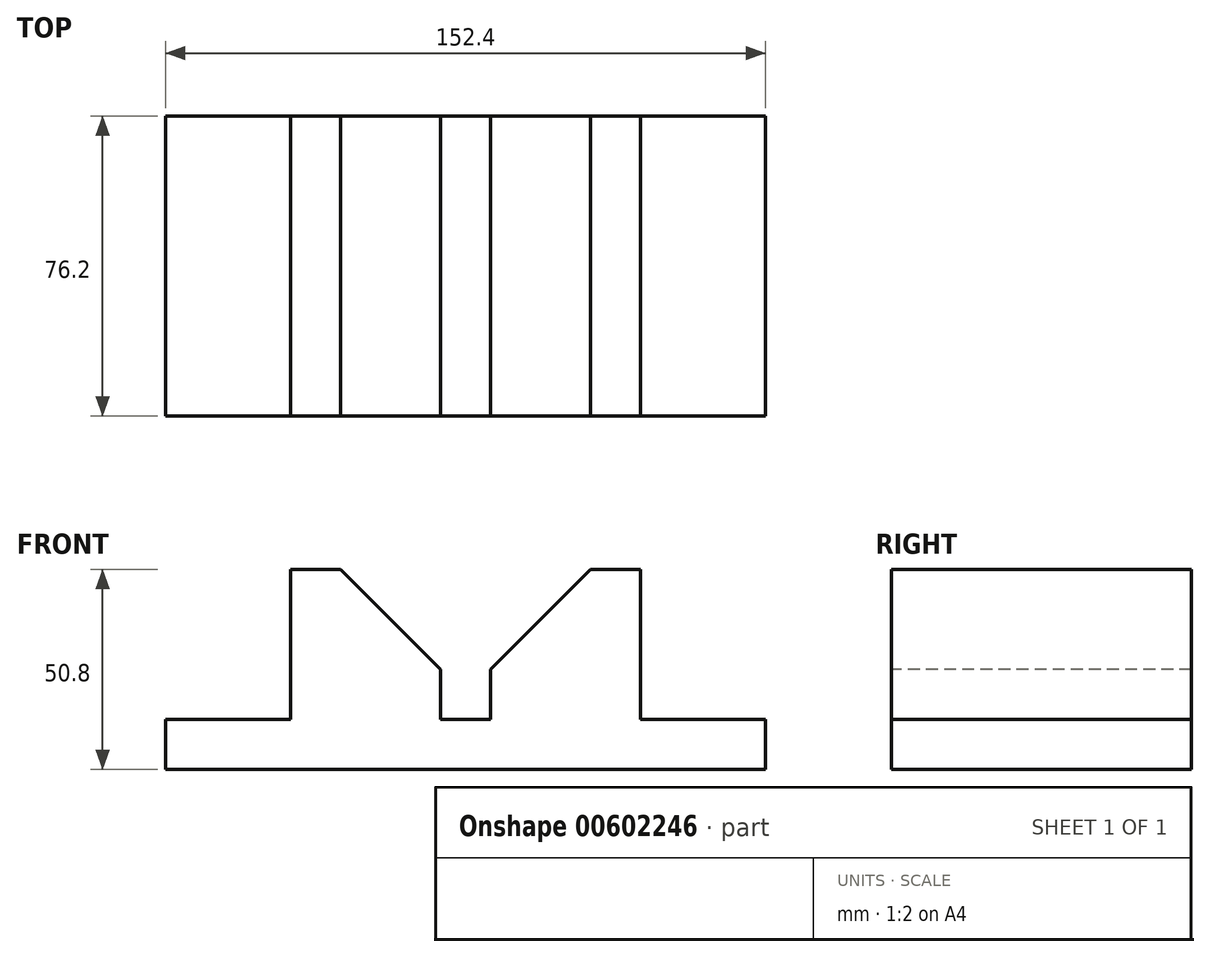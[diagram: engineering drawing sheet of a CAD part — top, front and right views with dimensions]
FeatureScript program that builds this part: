
annotation { "Feature Type Name" : "Feature", "Feature Type Description" : "" }
export const myFeature = defineFeature(function(context is Context, id is Id, definition is map)
    precondition{}
    {
        {
            var Q0;
            Q0=qCreatedBy(makeId("Front.planeOp"),FACE);
            var sketch = newSketch(context, id + "F0", { "sketchPlane" : qUnion([Q0])});
            skLineSegment(sketch, "E0.bottom", {"start": v(0, 0) * mm, "end": v(152.4, 0) * mm});
            skLineSegment(sketch, "E0.top", {"start": v(0, 50.8) * mm, "end": v(152.4, 50.8) * mm});
            skLineSegment(sketch, "E0.left", {"start": v(0, 0) * mm, "end": v(0, 50.8) * mm});
            skLineSegment(sketch, "E0.right", {"start": v(152.4, 0) * mm, "end": v(152.4, 50.8) * mm});
            skSolve(sketch);
        }
        {
            var Q0;
            Q0 = qSketchRegion(id + "F0", true);
            extrude(context, id + "F1", {"entities" : qUnion([Q0]), "oppositeDirection" : true, "depth" : 76.2 * mm, "offsetDistance" : 25.4 * mm});
        }
        {
            var Q0;
            Q0=makeQuery(id+"F1.opExtrude","CAP_FACE",FACE,{"disambiguationData":[OSD([sQuery(id+"F0.wireOp",EDGE,"E0.bottom"),sQuery(id+"F0.wireOp",EDGE,"E0.top"),sQuery(id+"F0.wireOp",EDGE,"E0.left"),sQuery(id+"F0.wireOp",EDGE,"E0.right")])],"isStart":true});
            var sketch = newSketch(context, id + "F2", { "sketchPlane" : qUnion([Q0])});
            skLineSegment(sketch, "E1", {"start": v(0, 0) * mm, "end": v(0, 12.7) * mm});
            skLineSegment(sketch, "E2", {"start": v(0, 12.7) * mm, "end": v(31.75, 12.7) * mm});
            skLineSegment(sketch, "E3", {"start": v(31.75, 12.7) * mm, "end": v(31.75, 50.8) * mm});
            skLineSegment(sketch, "E4", {"start": v(69.85, 12.7) * mm, "end": v(82.55, 12.7) * mm});
            skLineSegment(sketch, "E5", {"start": v(120.65, 50.8) * mm, "end": v(120.65, 12.7) * mm});
            skLineSegment(sketch, "E6", {"start": v(120.65, 12.7) * mm, "end": v(152.4, 12.7) * mm});
            skLineSegment(sketch, "E7", {"start": v(69.85, 12.7) * mm, "end": v(69.85, 25.4) * mm});
            skLineSegment(sketch, "E8", {"start": v(82.55, 12.7) * mm, "end": v(82.55, 25.4) * mm});
            skLineSegment(sketch, "E9", {"start": v(31.75, 50.8) * mm, "end": v(44.45, 50.8) * mm});
            skLineSegment(sketch, "E10", {"start": v(120.65, 50.8) * mm, "end": v(107.95, 50.8) * mm});
            skLineSegment(sketch, "E11", {"start": v(44.45, 50.8) * mm, "end": v(69.85, 25.4) * mm});
            skLineSegment(sketch, "E12", {"start": v(82.55, 25.4) * mm, "end": v(107.95, 50.8) * mm});
            skLineSegment(sketch, "E13", {"start": v(107.95, 50.8) * mm, "end": v(120.65, 50.8) * mm});
            skSolve(sketch);
        }
        {
            var Q0;
            {var subQ0=sQuery(id+"F2.wireOp",EDGE,"E2");Q0=makeQuery(id+"F2.imprint","IMPRINT",FACE,{"disambiguationData":[TD([[makeQuery(id+"F2.imprint","IMPRINT",EDGE,{"derivedFrom":subQ0}),1.0]])]});}
            var Q1;
            Q1=makeQuery(id+"F2.imprint","IMPRINT",FACE,{"disambiguationData":[TD([[makeQuery(id+"F2.imprint","IMPRINT",EDGE,{"derivedFrom":sQuery(id+"F2.wireOp",EDGE,"E7")}),-1.0]])]});
            var Q2;
            {var subQ0=sQuery(id+"F2.wireOp",EDGE,"E5");Q2=makeQuery(id+"F2.imprint","IMPRINT",FACE,{"disambiguationData":[TD([[makeQuery(id+"F2.imprint","IMPRINT",EDGE,{"derivedFrom":subQ0}),1.0]])]});}
            extrude(context, id + "F3", {"entities" : qUnion([Q0, Q1, Q2]), "operationType" : NewBodyOperationType.REMOVE, "oppositeDirection" : true, "depth" : 76.2 * mm, "offsetDistance" : 25.4 * mm});
        }
    });
